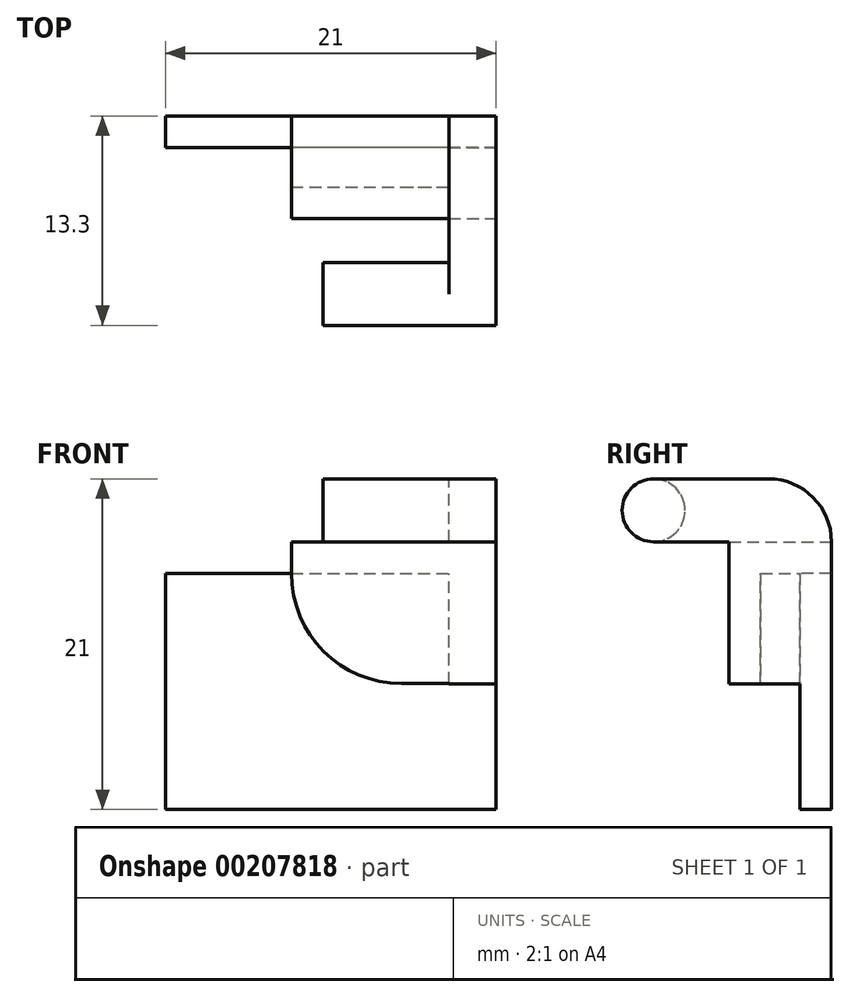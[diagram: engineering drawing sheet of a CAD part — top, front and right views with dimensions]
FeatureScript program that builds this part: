
annotation { "Feature Type Name" : "Feature", "Feature Type Description" : "" }
export const myFeature = defineFeature(function(context is Context, id is Id, definition is map)
    precondition{}
    {
        {
            var Q0;
            Q0=qCreatedBy(makeId("Front.planeOp"),FACE);
            var sketch = newSketch(context, id + "F0", { "sketchPlane" : qUnion([Q0])});
            skArc(sketch, "E0", {"start": v(-7, 0) * mm, "mid": v(-4.95, -4.95) * mm, "end": v(0, -7) * mm});
            skLineSegment(sketch, "E1", {"start": v(-7, 0) * mm, "end": v(0, 0) * mm});
            skLineSegment(sketch, "E2", {"start": v(0, 0) * mm, "end": v(6, 0) * mm});
            skLineSegment(sketch, "E3", {"start": v(6, 0) * mm, "end": v(6, -7) * mm});
            skLineSegment(sketch, "E4", {"start": v(0, -7) * mm, "end": v(6, -7) * mm});
            skSolve(sketch);
        }
        {
            var Q0;
            Q0=qCreatedBy(makeId("Front.planeOp"),FACE);
            cPlane(context, id + "F1", {"entities" : qUnion([Q0]), "cplaneType" : CPlaneType.OFFSET, "offset" : 2.5 * mm, "oppositeDirection" : true, "width" : 150 * mm, "height" : 150 * mm});
        }
        {
            var Q0;
            Q0=qCreatedBy(id+"F1.planeOp",FACE);
            var sketch = newSketch(context, id + "F2", { "sketchPlane" : qUnion([Q0])});
            skLineSegment(sketch, "E5.bottom", {"start": v(0, 0) * mm, "end": v(-15, 0) * mm});
            skLineSegment(sketch, "E5.top", {"start": v(0, -15) * mm, "end": v(-15, -15) * mm});
            skLineSegment(sketch, "E5.right", {"start": v(-15, 0) * mm, "end": v(-15, -15) * mm});
            skLineSegment(sketch, "E6.bottom", {"start": v(0, 0) * mm, "end": v(6, 0) * mm});
            skLineSegment(sketch, "E6.top", {"start": v(0, -15) * mm, "end": v(6, -15) * mm});
            skLineSegment(sketch, "E6.right", {"start": v(6, 0) * mm, "end": v(6, -15) * mm});
            skSolve(sketch);
        }
        {
            var Q0;
            Q0=makeQuery(id+"F0.imprint","IMPRINT",FACE,{"disambiguationData":[TD([[makeQuery(id+"F0.imprint","IMPRINT",EDGE,{"derivedFrom":sQuery(id+"F0.wireOp",EDGE,"E0")}),1.0]])]});
            extrude(context, id + "F3", {"entities" : qUnion([Q0]), "depth" : 2 * mm});
        }
        {
            var Q0;
            Q0=makeQuery(id+"F2.imprint","IMPRINT",FACE,{"disambiguationData":[TD([[makeQuery(id+"F2.imprint","IMPRINT",EDGE,{"derivedFrom":sQuery(id+"F2.wireOp",EDGE,"E5.bottom")}),1.0]])]});
            extrude(context, id + "F4", {"entities" : qUnion([Q0]), "oppositeDirection" : true, "depth" : 2 * mm});
        }
        {
            var Q0;
            Q0=makeQuery(id+"F3.opExtrude","SWEPT_FACE",FACE,{"disambiguationData":[OSD([sQuery(id+"F0.wireOp",EDGE,"E1")])]});
            var sketch = newSketch(context, id + "F5", { "sketchPlane" : qUnion([Q0])});
            skPoint(sketch, "E7.0", {"position": v(6, 4.5) * mm});
            skLineSegment(sketch, "E8.bottom", {"start": v(6, 4.5) * mm, "end": v(-7, 4.5) * mm});
            skLineSegment(sketch, "E8.top", {"start": v(6, -2) * mm, "end": v(-7, -2) * mm});
            skLineSegment(sketch, "E8.left", {"start": v(6, 4.5) * mm, "end": v(6, -2) * mm});
            skLineSegment(sketch, "E8.right", {"start": v(-7, 4.5) * mm, "end": v(-7, -2) * mm});
            skSolve(sketch);
        }
        {
            var Q0;
            {var subQ0=sQuery(id+"F5.wireOp",EDGE,"E8.bottom");Q0=makeQuery(id+"F5.imprint","IMPRINT",FACE,{"disambiguationData":[TD([[makeQuery(id+"F5.imprint","IMPRINT",EDGE,{"derivedFrom":subQ0}),1.0]])]});}
            var Q1;
            {var subQ0=sQuery(id+"F5.wireOp",EDGE,"E8.top");Q1=makeQuery(id+"F5.imprint","IMPRINT",FACE,{"disambiguationData":[TD([[makeQuery(id+"F5.imprint","IMPRINT",EDGE,{"derivedFrom":subQ0}),1.0]])]});}
            extrude(context, id + "F6", {"entities" : qUnion([Q0, Q1]), "depth" : 2 * mm});
        }
        {
            var Q0;
            Q0=makeQuery(id+"F3.opExtrude","SWEPT_FACE",FACE,{"disambiguationData":[OSD([sQuery(id+"F0.wireOp",EDGE,"E3")])]});
            var sketch = newSketch(context, id + "F7", { "sketchPlane" : qUnion([Q0])});
            skCircle(sketch, "E9", {"center": v(-6.8, 4) * mm, "radius": 2 * mm});
            skSolve(sketch);
        }
        {
            var Q0;
            Q0=makeQuery(id+"F7.imprint","IMPRINT",FACE,{"disambiguationData":[TD([[makeQuery(id+"F7.imprint","IMPRINT",EDGE,{"derivedFrom":sQuery(id+"F7.wireOp",EDGE,"E9")}),1.0]])]});
            extrude(context, id + "F8", {"entities" : qUnion([Q0]), "oppositeDirection" : true, "depth" : 11 * mm});
        }
        {
            var Q0;
            Q0=makeQuery(id+"F8.opExtrude","CAP_FACE",FACE,{"disambiguationData":[OSD([sQuery(id+"F7.wireOp",EDGE,"E9")])],"isStart":true});
            var sketch = newSketch(context, id + "F9", { "sketchPlane" : qUnion([Q0])});
            skLineSegment(sketch, "E10", {"start": v(-2, 2) * mm, "end": v(-6.8, 2) * mm});
            skLineSegment(sketch, "E11", {"start": v(4.5, 2) * mm, "end": v(4.5, 2) * mm});
            skLineSegment(sketch, "E12", {"start": v(0.5, 6) * mm, "end": v(-6.8, 6) * mm});
            skLineSegment(sketch, "E13", {"start": v(-2, 2) * mm, "end": v(-2, -7.03) * mm});
            skLineSegment(sketch, "E14", {"start": v(-2, -7.03) * mm, "end": v(4.5, -7.03) * mm});
            skLineSegment(sketch, "E15", {"start": v(4.5, 2) * mm, "end": v(4.5, -7.03) * mm});
            skPoint(sketch, "E16.visualSharp", {"position": v(4.5, 6) * mm});
            skArc(sketch, "E16.filletArc", {"start": v(4.5, 2) * mm, "mid": v(3.33, 4.83) * mm, "end": v(0.5, 6) * mm});
            skSolve(sketch);
        }
        {
            var Q0;
            {var subQ1=sQuery(id+"F9.wireOp",EDGE,"E10");Q0=makeQuery(id+"F9.imprint","IMPRINT",FACE,{"disambiguationData":[TD([[makeQuery(id+"F9.imprint","IMPRINT",EDGE,{"derivedFrom":subQ1}),-1.0]])]});}
            extrude(context, id + "F10", {"entities" : qUnion([Q0]), "operationType" : NewBodyOperationType.ADD, "oppositeDirection" : true, "depth" : 3 * mm});
        }
    });
